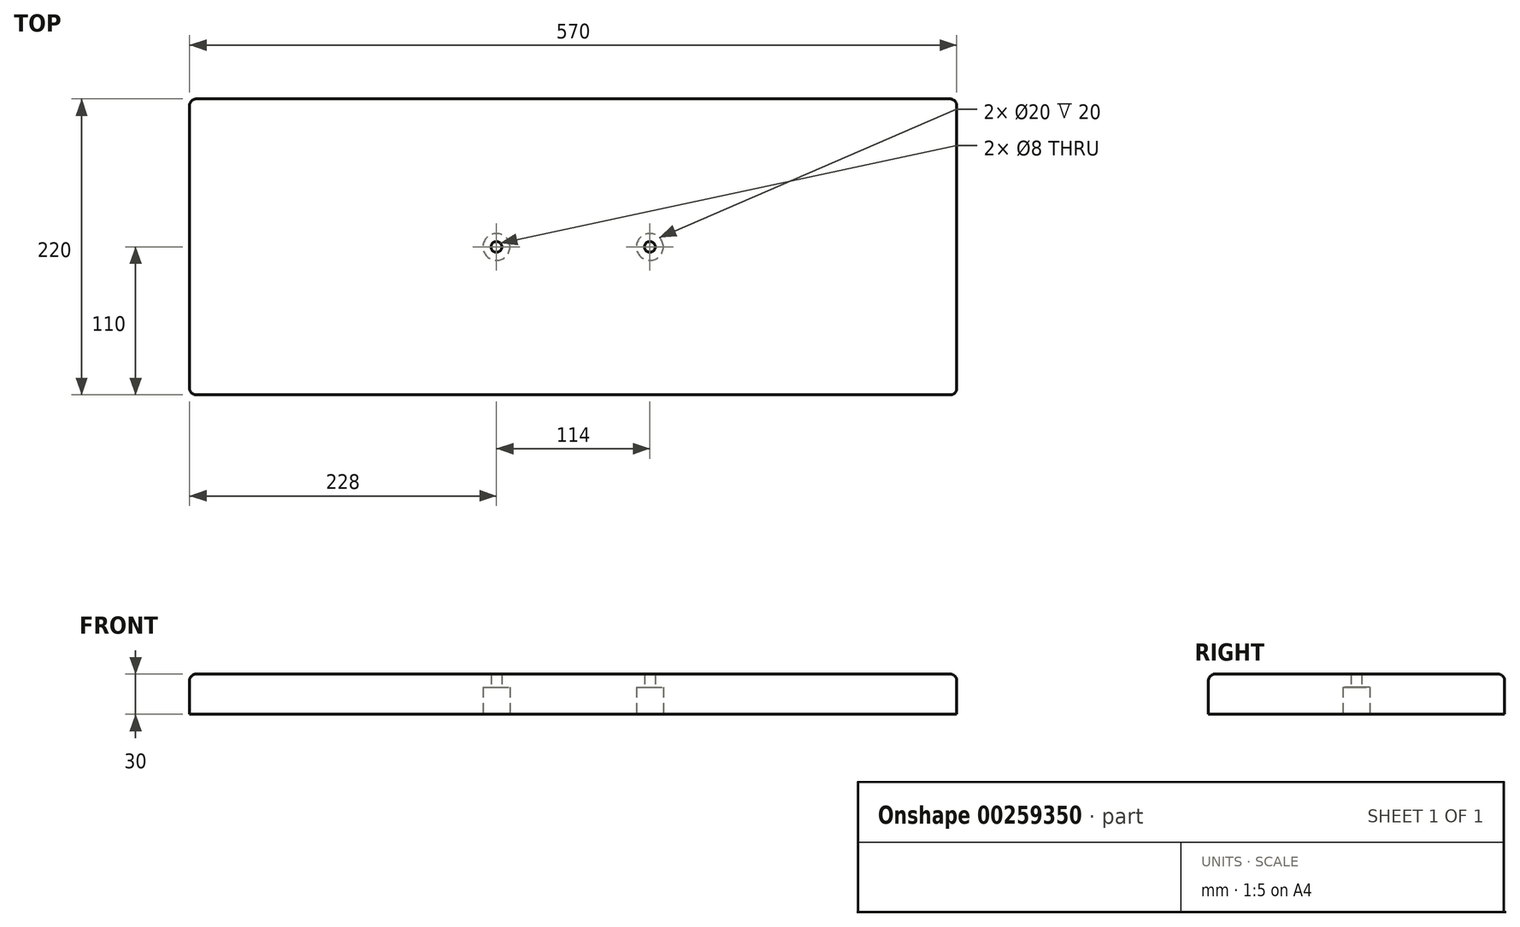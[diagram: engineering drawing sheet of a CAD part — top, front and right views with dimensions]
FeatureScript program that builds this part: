
annotation { "Feature Type Name" : "Feature", "Feature Type Description" : "" }
export const myFeature = defineFeature(function(context is Context, id is Id, definition is map)
    precondition{}
    {
        {
            var Q0;
            Q0=qCreatedBy(makeId("Top.planeOp"),FACE);
            var sketch = newSketch(context, id + "F0", { "sketchPlane" : qUnion([Q0])});
            skLineSegment(sketch, "E0", {"start": v(-285, 0) * mm, "end": v(-285, 110) * mm});
            skLineSegment(sketch, "E1", {"start": v(-285, 110) * mm, "end": v(0, 110) * mm});
            skLineSegment(sketch, "E2.MirrorCS", {"start": v(280, 110) * mm, "end": v(0, 110) * mm});
            skLineSegment(sketch, "E3.MirrorCS", {"start": v(285, 0) * mm, "end": v(285, 105) * mm});
            skLineSegment(sketch, "E4.MirrorCS", {"start": v(-285, 0) * mm, "end": v(-285, -110) * mm});
            skLineSegment(sketch, "E5.MirrorCS", {"start": v(-285, -110) * mm, "end": v(0, -110) * mm});
            skLineSegment(sketch, "E6.MirrorCS", {"start": v(285, -110) * mm, "end": v(0, -110) * mm});
            skLineSegment(sketch, "E7.MirrorCS", {"start": v(285, 0) * mm, "end": v(285, -110) * mm});
            skPoint(sketch, "E8.visualSharp", {"position": v(285, 110) * mm});
            skArc(sketch, "E8.filletArc", {"start": v(285, 105) * mm, "mid": v(283.54, 108.54) * mm, "end": v(280, 110) * mm});
            skPoint(sketch, "E9.MirrorP", {"position": v(-285, 110) * mm});
            skArc(sketch, "E10.MirrorCS", {"start": v(-285, 105) * mm, "mid": v(-283.54, 108.54) * mm, "end": v(-280, 110) * mm});
            skArc(sketch, "E11.MirrorCS", {"start": v(-285, -105) * mm, "mid": v(-283.54, -108.54) * mm, "end": v(-280, -110) * mm});
            skPoint(sketch, "E12.MirrorP", {"position": v(-285, -110) * mm});
            skArc(sketch, "E13.MirrorCS", {"start": v(285, -105) * mm, "mid": v(283.54, -108.54) * mm, "end": v(280, -110) * mm});
            skPoint(sketch, "E14.MirrorP", {"position": v(285, -110) * mm});
            skSolve(sketch);
        }
        {
            var Q0;
            {var subQ9=sQuery(id+"F0.wireOp",EDGE,"E2.MirrorCS");Q0=makeQuery(id+"F0.imprint","IMPRINT",FACE,{"disambiguationData":[TD([[makeQuery(id+"F0.imprint","IMPRINT",EDGE,{"derivedFrom":subQ9}),1.0]])]});}
            extrude(context, id + "F1", {"entities" : qUnion([Q0]), "depth" : 30 * mm});
        }
        {
            var Q0;
            Q0=makeQuery(id+"F1.opExtrude","CAP_FACE",FACE,{"disambiguationData":[OSD([sQuery(id+"F0.wireOp",EDGE,"E0"),sQuery(id+"F0.wireOp",EDGE,"E1"),sQuery(id+"F0.wireOp",EDGE,"E2.MirrorCS"),sQuery(id+"F0.wireOp",EDGE,"E3.MirrorCS"),sQuery(id+"F0.wireOp",EDGE,"E4.MirrorCS"),sQuery(id+"F0.wireOp",EDGE,"E5.MirrorCS"),sQuery(id+"F0.wireOp",EDGE,"E6.MirrorCS"),sQuery(id+"F0.wireOp",EDGE,"E7.MirrorCS"),sQuery(id+"F0.wireOp",EDGE,"E8.filletArc"),sQuery(id+"F0.wireOp",EDGE,"E10.MirrorCS"),sQuery(id+"F0.wireOp",EDGE,"E11.MirrorCS"),sQuery(id+"F0.wireOp",EDGE,"E13.MirrorCS")])],"isStart":false});
            var Q1;
            Q1=makeQuery(id+"F1.opExtrude","CAP_EDGE",EDGE,{"disambiguationData":[OSD([sQuery(id+"F0.wireOp",EDGE,"E5.MirrorCS"),sQuery(id+"F0.wireOp",EDGE,"E6.MirrorCS")])],"isStart":false});
            var Q2;
            Q2=makeQuery(id+"F1.opExtrude","CAP_EDGE",EDGE,{"disambiguationData":[OSD([sQuery(id+"F0.wireOp",EDGE,"E0"),sQuery(id+"F0.wireOp",EDGE,"E4.MirrorCS")])],"isStart":false});
            var Q3;
            Q3=makeQuery(id+"F1.opExtrude","CAP_EDGE",EDGE,{"disambiguationData":[OSD([sQuery(id+"F0.wireOp",EDGE,"E1"),sQuery(id+"F0.wireOp",EDGE,"E2.MirrorCS")])],"isStart":false});
            var Q4;
            Q4=makeQuery(id+"F1.opExtrude","CAP_EDGE",EDGE,{"disambiguationData":[OSD([sQuery(id+"F0.wireOp",EDGE,"E3.MirrorCS"),sQuery(id+"F0.wireOp",EDGE,"E7.MirrorCS")])],"isStart":false});
            fillet(context, id + "F2", {"entities" : qUnion([Q0, Q1, Q2, Q3, Q4]), "radius" : 5 * mm, "tangentPropagation" : true, "allowEdgeOverflow" : false});
        }
        {
            var Q0;
            Q0=makeQuery(id+"F1.opExtrude","CAP_FACE",FACE,{"disambiguationData":[OSD([sQuery(id+"F0.wireOp",EDGE,"E0"),sQuery(id+"F0.wireOp",EDGE,"E1"),sQuery(id+"F0.wireOp",EDGE,"E2.MirrorCS"),sQuery(id+"F0.wireOp",EDGE,"E3.MirrorCS"),sQuery(id+"F0.wireOp",EDGE,"E4.MirrorCS"),sQuery(id+"F0.wireOp",EDGE,"E5.MirrorCS"),sQuery(id+"F0.wireOp",EDGE,"E6.MirrorCS"),sQuery(id+"F0.wireOp",EDGE,"E7.MirrorCS"),sQuery(id+"F0.wireOp",EDGE,"E8.filletArc"),sQuery(id+"F0.wireOp",EDGE,"E10.MirrorCS"),sQuery(id+"F0.wireOp",EDGE,"E11.MirrorCS"),sQuery(id+"F0.wireOp",EDGE,"E13.MirrorCS")])],"isStart":true});
            var sketch = newSketch(context, id + "F3", { "sketchPlane" : qUnion([Q0])});
            skLineSegment(sketch, "E15", {"start": v(0, 0) * mm, "end": v(57, 0) * mm, "construction": true});
            skCircle(sketch, "E16", {"center": v(0, 0) * mm, "radius": 60 * mm, "construction": true});
            skCircle(sketch, "E17", {"center": v(57, 0) * mm, "radius": 4 * mm});
            skCircle(sketch, "E18", {"center": v(57, 0) * mm, "radius": 10 * mm});
            skCircle(sketch, "E19.MirrorC", {"center": v(-57, 0) * mm, "radius": 10 * mm});
            skCircle(sketch, "E20.MirrorC", {"center": v(-57, 0) * mm, "radius": 4 * mm});
            skLineSegment(sketch, "E21.MirrorCS", {"start": v(0, 0) * mm, "end": v(-57, 0) * mm, "construction": true});
            skSolve(sketch);
        }
        {
            var Q0;
            Q0 = qSketchRegion(id + "F3", true);
            extrude(context, id + "F4", {"entities" : qUnion([Q0]), "operationType" : NewBodyOperationType.REMOVE, "oppositeDirection" : true, "depth" : 20 * mm});
        }
        {
            var Q0;
            Q0=makeQuery(id+"F4.boolean.opBoolean","SPLIT",FACE,{"disambiguationData":[TD([makeQuery(id+"F4.opExtrude","SWEPT_FACE",FACE,{"disambiguationData":[OSD([sQuery(id+"F3.wireOp",EDGE,"E17")])]})])],"derivedFrom":makeQuery(id+"F1.opExtrude","CAP_FACE",FACE,{"disambiguationData":[OSD([sQuery(id+"F0.wireOp",EDGE,"E0"),sQuery(id+"F0.wireOp",EDGE,"E1"),sQuery(id+"F0.wireOp",EDGE,"E2.MirrorCS"),sQuery(id+"F0.wireOp",EDGE,"E3.MirrorCS"),sQuery(id+"F0.wireOp",EDGE,"E4.MirrorCS"),sQuery(id+"F0.wireOp",EDGE,"E5.MirrorCS"),sQuery(id+"F0.wireOp",EDGE,"E6.MirrorCS"),sQuery(id+"F0.wireOp",EDGE,"E7.MirrorCS"),sQuery(id+"F0.wireOp",EDGE,"E8.filletArc"),sQuery(id+"F0.wireOp",EDGE,"E10.MirrorCS"),sQuery(id+"F0.wireOp",EDGE,"E11.MirrorCS"),sQuery(id+"F0.wireOp",EDGE,"E13.MirrorCS")])],"isStart":true})});
            var Q1;
            Q1=makeQuery(id+"F4.boolean.opBoolean","SPLIT",FACE,{"disambiguationData":[TD([makeQuery(id+"F4.opExtrude","SWEPT_FACE",FACE,{"disambiguationData":[OSD([sQuery(id+"F3.wireOp",EDGE,"E20.MirrorC")])]})])],"derivedFrom":makeQuery(id+"F1.opExtrude","CAP_FACE",FACE,{"disambiguationData":[OSD([sQuery(id+"F0.wireOp",EDGE,"E0"),sQuery(id+"F0.wireOp",EDGE,"E1"),sQuery(id+"F0.wireOp",EDGE,"E2.MirrorCS"),sQuery(id+"F0.wireOp",EDGE,"E3.MirrorCS"),sQuery(id+"F0.wireOp",EDGE,"E4.MirrorCS"),sQuery(id+"F0.wireOp",EDGE,"E5.MirrorCS"),sQuery(id+"F0.wireOp",EDGE,"E6.MirrorCS"),sQuery(id+"F0.wireOp",EDGE,"E7.MirrorCS"),sQuery(id+"F0.wireOp",EDGE,"E8.filletArc"),sQuery(id+"F0.wireOp",EDGE,"E10.MirrorCS"),sQuery(id+"F0.wireOp",EDGE,"E11.MirrorCS"),sQuery(id+"F0.wireOp",EDGE,"E13.MirrorCS")])],"isStart":true})});
            extrude(context, id + "F5", {"entities" : qUnion([Q0, Q1]), "operationType" : NewBodyOperationType.REMOVE, "endBound" : BoundingType.THROUGH_ALL, "oppositeDirection" : true, "depth" : 25 * mm});
        }
    });
